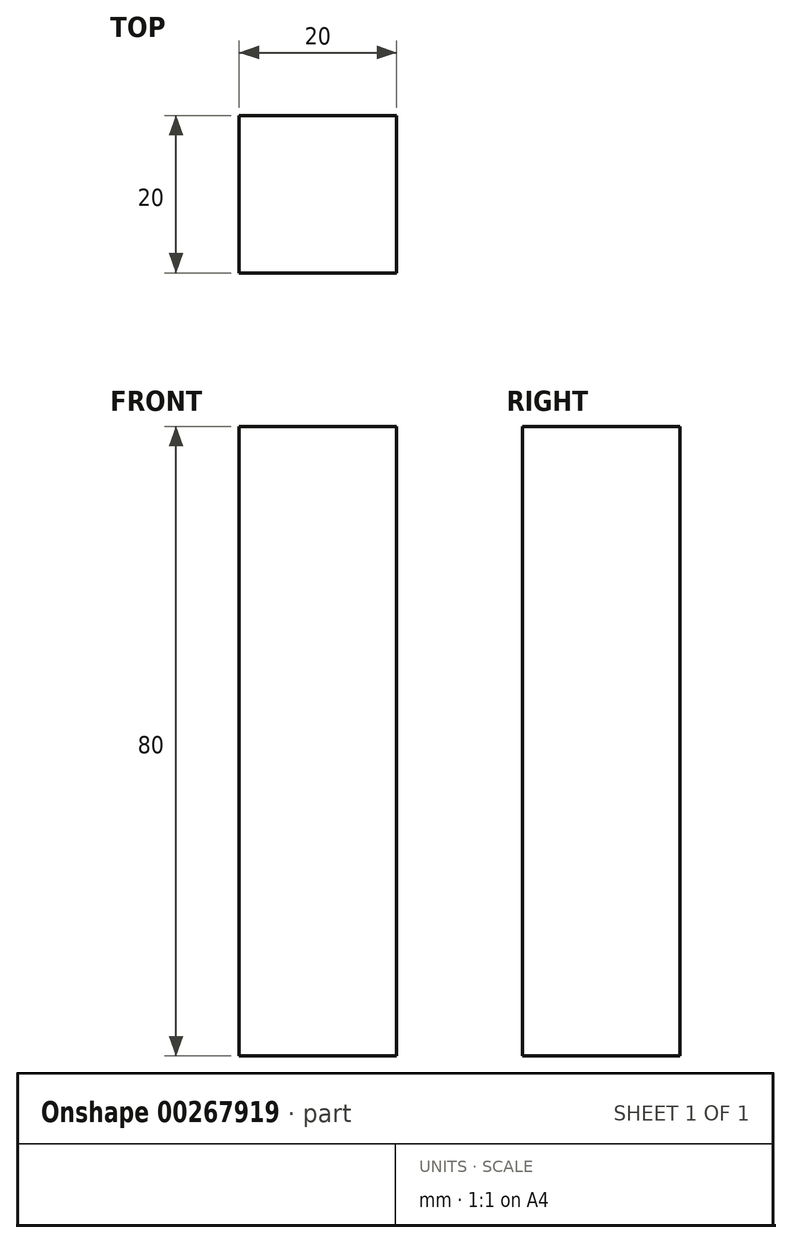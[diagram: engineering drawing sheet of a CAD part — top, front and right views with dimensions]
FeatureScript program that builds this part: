
annotation { "Feature Type Name" : "Feature", "Feature Type Description" : "" }
export const myFeature = defineFeature(function(context is Context, id is Id, definition is map)
    precondition{}
    {
        {
            var Q0;
            Q0=qCreatedBy(makeId("Top.planeOp"),FACE);
            var sketch = newSketch(context, id + "F0", { "sketchPlane" : qUnion([Q0])});
            skLineSegment(sketch, "E0.bottom", {"start": v(-42.65, 17.43) * mm, "end": v(-22.65, 17.43) * mm});
            skLineSegment(sketch, "E0.top", {"start": v(-42.65, -2.57) * mm, "end": v(-22.65, -2.57) * mm});
            skLineSegment(sketch, "E0.left", {"start": v(-42.65, 17.43) * mm, "end": v(-42.65, -2.57) * mm});
            skLineSegment(sketch, "E0.right", {"start": v(-22.65, 17.43) * mm, "end": v(-22.65, -2.57) * mm});
            skSolve(sketch);
        }
        {
            var Q0;
            Q0=makeQuery(id+"F0.imprint","IMPRINT",FACE,{"disambiguationData":[TD([[makeQuery(id+"F0.imprint","IMPRINT",EDGE,{"derivedFrom":sQuery(id+"F0.wireOp",EDGE,"E0.bottom")}),-1.0]])]});
            extrude(context, id + "F1", {"entities" : qUnion([Q0]), "depth" : 80 * mm});
        }
    });
